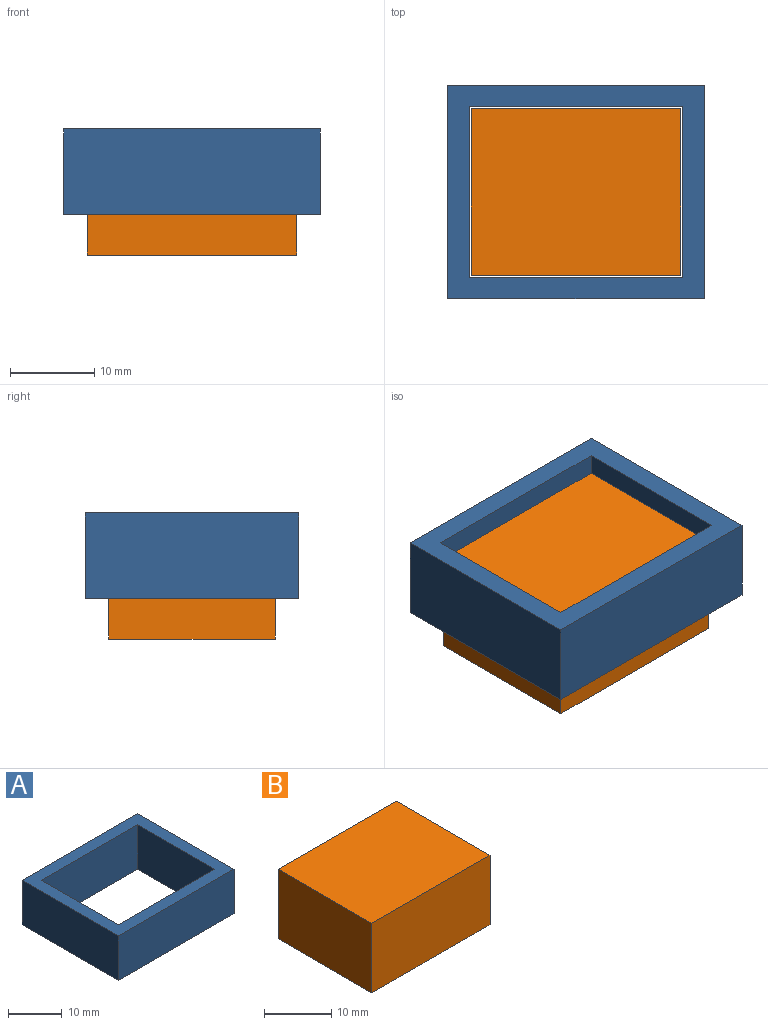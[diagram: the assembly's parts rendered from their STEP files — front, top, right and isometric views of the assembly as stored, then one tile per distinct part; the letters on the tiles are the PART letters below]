
ASSEMBLY  parts=2 mates=1
PART A: 10 faces, bbox 30.5x25.4x10.2 mm
  f0: plane 30.48x10.16mm, normal (0,1,0), area 309.7mm2, adj f1,f7,f8,f9
  f1: plane 25.4x10.16mm, normal (-1,0,0), area 258.1mm2, adj f0,f2,f8,f9
  f2: plane 30.48x10.16mm, normal (0,-1,0), area 309.7mm2, adj f1,f7,f8,f9
  f3: plane 20.32x10.16mm, normal (1,0,0), area 206.5mm2, adj f4,f6,f8,f9
  f4: plane 25.4x10.16mm, normal (0,-1,0), area 258.1mm2, adj f3,f5,f8,f9
  f5: plane 20.32x10.16mm, normal (-1,0,0), area 206.5mm2, adj f4,f6,f8,f9
  f6: plane 25.4x10.16mm, normal (0,1,0), area 258.1mm2, adj f3,f5,f8,f9
  f7: plane 25.4x10.16mm, normal (1,0,0), area 258.1mm2, adj f0,f2,f8,f9
  f8: plane 30.48x25.4mm, normal (0,0,1), area 258.1mm2, adj f0,f1,f2,f3,f4,f5,f6,f7
  f9: plane 30.48x25.4mm, normal (0,0,-1), area 258.1mm2, adj f0,f1,f2,f3,f4,f5,f6,f7
PART B: 6 faces, bbox 24.9x19.8x12.7 mm
  f0: plane 24.89x12.7mm, normal (0,1,0), area 316.1mm2, adj f1,f3,f4,f5
  f1: plane 19.81x12.7mm, normal (-1,0,0), area 251.6mm2, adj f0,f2,f4,f5
  f2: plane 24.89x12.7mm, normal (0,-1,0), area 316.1mm2, adj f1,f3,f4,f5
  f3: plane 19.81x12.7mm, normal (1,0,0), area 251.6mm2, adj f0,f2,f4,f5
  f4: plane 24.89x19.81mm, normal (0,0,1), area 493.2mm2, adj f0,f1,f2,f3
  f5: plane 24.89x19.81mm, normal (0,0,-1), area 493.2mm2, adj f0,f1,f2,f3
PLACE A rot(axis=(1,0,0),180deg) t=(-1.18,-21.16,80.52)mm
PLACE B t=(-1.18,-21.16,76.95)mm
MATE slider B.f4 <-> A.f9  axis (0,0,1) through (-1.18,-21.16,83.3)mm
